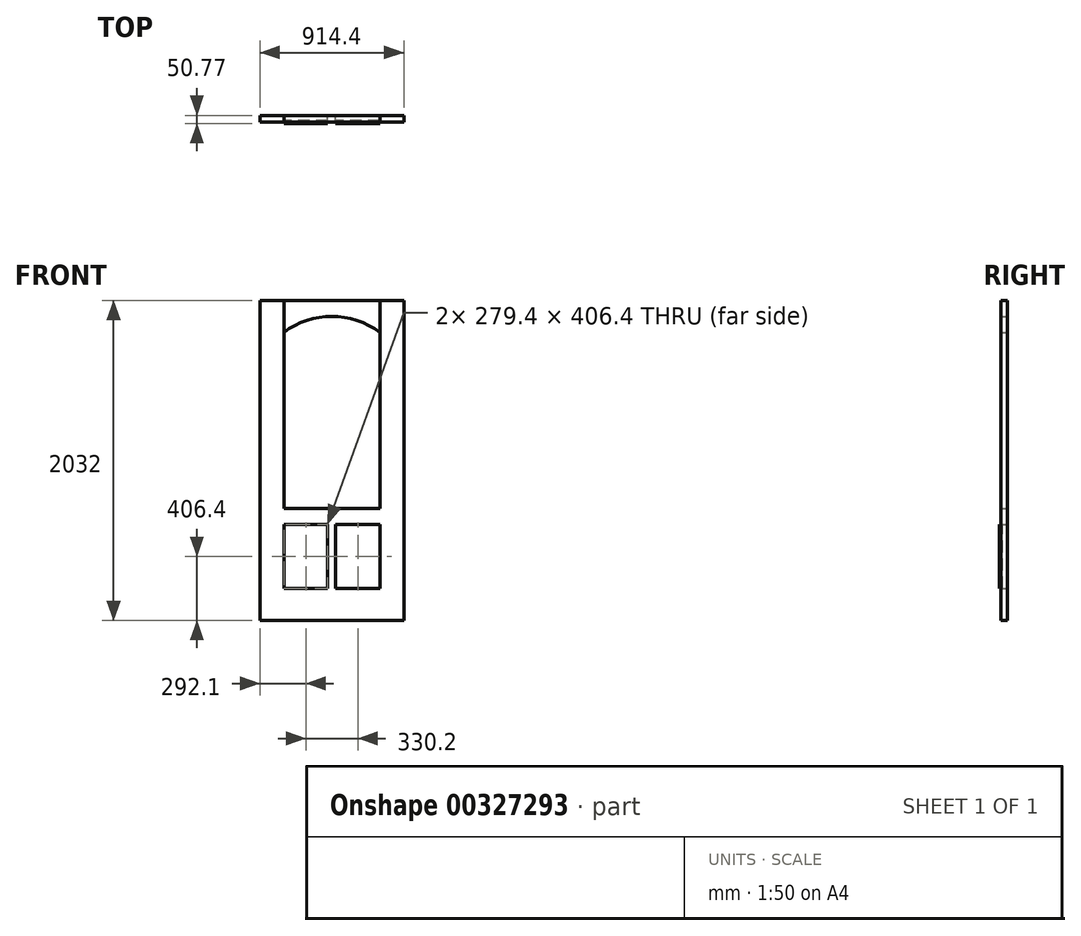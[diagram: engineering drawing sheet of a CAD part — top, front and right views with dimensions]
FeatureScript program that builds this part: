
annotation { "Feature Type Name" : "Feature", "Feature Type Description" : "" }
export const myFeature = defineFeature(function(context is Context, id is Id, definition is map)
    precondition{}
    {
        {
            var Q0;
            Q0=qCreatedBy(makeId("Front.planeOp"),FACE);
            var sketch = newSketch(context, id + "F0", { "sketchPlane" : qUnion([Q0])});
            skLineSegment(sketch, "E0.bottom", {"start": v(0, 0) * mm, "end": v(914.4, 0) * mm});
            skLineSegment(sketch, "E0.top", {"start": v(0, 2032) * mm, "end": v(152.4, 2032) * mm});
            skLineSegment(sketch, "E0.left", {"start": v(0, 0) * mm, "end": v(0, 2032) * mm});
            skLineSegment(sketch, "E0.right", {"start": v(914.4, 0) * mm, "end": v(914.4, 2032) * mm});
            skLineSegment(sketch, "E1", {"start": v(152.4, 2032) * mm, "end": v(152.4, 711.2) * mm});
            skLineSegment(sketch, "E2", {"start": v(152.4, 711.2) * mm, "end": v(762, 711.2) * mm});
            skLineSegment(sketch, "E3", {"start": v(762, 711.2) * mm, "end": v(762, 2032) * mm});
            skLineSegment(sketch, "E4.trimOffspring", {"start": v(762, 2032) * mm, "end": v(914.4, 2032) * mm});
            skSolve(sketch);
        }
        {
            var Q0;
            Q0=makeQuery(id+"F0.imprint","IMPRINT",FACE,{"disambiguationData":[TD([[makeQuery(id+"F0.imprint","IMPRINT",EDGE,{"derivedFrom":sQuery(id+"F0.wireOp",EDGE,"E0.bottom")}),1.0]])]});
            extrude(context, id + "F1", {"entities" : qUnion([Q0]), "depth" : 41.27 * mm});
        }
        {
            var Q0;
            Q0=makeQuery(id+"F1.opExtrude","CAP_FACE",FACE,{"disambiguationData":[OSD([sQuery(id+"F0.wireOp",EDGE,"E0.bottom"),sQuery(id+"F0.wireOp",EDGE,"E0.top"),sQuery(id+"F0.wireOp",EDGE,"E0.left"),sQuery(id+"F0.wireOp",EDGE,"E0.right"),sQuery(id+"F0.wireOp",EDGE,"E1"),sQuery(id+"F0.wireOp",EDGE,"E2"),sQuery(id+"F0.wireOp",EDGE,"E3"),sQuery(id+"F0.wireOp",EDGE,"E4.trimOffspring")])],"isStart":false});
            cPlane(context, id + "F2", {"entities" : qUnion([Q0]), "cplaneType" : CPlaneType.OFFSET, "offset" : 13 / 406.4 * mm, "oppositeDirection" : true, "width" : 152.4 * mm, "height" : 152.4 * mm});
        }
        {
            var Q0;
            Q0=qCreatedBy(makeId("Front.planeOp"),FACE);
            var sketch = newSketch(context, id + "F3", { "sketchPlane" : qUnion([Q0])});
            skLineSegment(sketch, "E5.0", {"start": v(152.4, 2032) * mm, "end": v(152.4, 711.2) * mm});
            skLineSegment(sketch, "E6.0", {"start": v(762, 711.2) * mm, "end": v(762, 2032) * mm});
            skLineSegment(sketch, "E7", {"start": v(152.4, 2032) * mm, "end": v(762, 2032) * mm});
            skLineSegment(sketch, "E8", {"start": v(152.4, 2032) * mm, "end": v(152.4, 1828.8) * mm});
            skLineSegment(sketch, "E9", {"start": v(762, 2032) * mm, "end": v(762, 1828.8) * mm});
            skLineSegment(sketch, "E10", {"start": v(152.4, 1930.4) * mm, "end": v(762, 1930.4) * mm, "construction": true});
            skArc(sketch, "E11", {"start": v(762, 1828.8) * mm, "mid": v(457.2, 1930.4) * mm, "end": v(152.4, 1828.8) * mm});
            skSolve(sketch);
        }
        {
            var Q0;
            Q0=makeQuery(id+"F3.imprint","IMPRINT",FACE,{"disambiguationData":[TD([[makeQuery(id+"F3.imprint","IMPRINT",EDGE,{"derivedFrom":sQuery(id+"F3.wireOp",EDGE,"E7")}),-1.0]])]});
            var Q1;
            Q1=makeQuery(id+"F1.opExtrude","CAP_FACE",FACE,{"disambiguationData":[OSD([sQuery(id+"F0.wireOp",EDGE,"E0.bottom"),sQuery(id+"F0.wireOp",EDGE,"E0.top"),sQuery(id+"F0.wireOp",EDGE,"E0.left"),sQuery(id+"F0.wireOp",EDGE,"E0.right"),sQuery(id+"F0.wireOp",EDGE,"E1"),sQuery(id+"F0.wireOp",EDGE,"E2"),sQuery(id+"F0.wireOp",EDGE,"E3"),sQuery(id+"F0.wireOp",EDGE,"E4.trimOffspring")])],"isStart":false});
            extrude(context, id + "F4", {"entities" : qUnion([Q0]), "endBound" : BoundingType.UP_TO_SURFACE, "endBoundEntityFace" : qUnion([Q1]), "depth" : 25.4 * mm});
        }
        {
            var Q0;
            Q0=qCreatedBy(makeId("Front.planeOp"),FACE);
            var sketch = newSketch(context, id + "F5", { "sketchPlane" : qUnion([Q0])});
            skLineSegment(sketch, "E12.bottom", {"start": v(152.4, 609.6) * mm, "end": v(431.8, 609.6) * mm});
            skLineSegment(sketch, "E12.top", {"start": v(152.4, 203.2) * mm, "end": v(431.8, 203.2) * mm});
            skLineSegment(sketch, "E12.left", {"start": v(152.4, 609.6) * mm, "end": v(152.4, 203.2) * mm});
            skLineSegment(sketch, "E12.right", {"start": v(431.8, 609.6) * mm, "end": v(431.8, 203.2) * mm});
            skLineSegment(sketch, "E13.0", {"start": v(152.4, 711.2) * mm, "end": v(762, 711.2) * mm});
            skLineSegment(sketch, "E14.bottom", {"start": v(482.6, 609.6) * mm, "end": v(762, 609.6) * mm});
            skLineSegment(sketch, "E14.top", {"start": v(482.6, 203.2) * mm, "end": v(762, 203.2) * mm});
            skLineSegment(sketch, "E14.left", {"start": v(482.6, 609.6) * mm, "end": v(482.6, 203.2) * mm});
            skLineSegment(sketch, "E14.right", {"start": v(762, 609.6) * mm, "end": v(762, 203.2) * mm});
            skSolve(sketch);
        }
        {
            var Q0;
            Q0=makeQuery(id+"F5.imprint","IMPRINT",FACE,{"disambiguationData":[TD([[makeQuery(id+"F5.imprint","IMPRINT",EDGE,{"derivedFrom":sQuery(id+"F5.wireOp",EDGE,"E14.bottom")}),-1.0]])]});
            var Q1;
            Q1=makeQuery(id+"F5.imprint","IMPRINT",FACE,{"disambiguationData":[TD([[makeQuery(id+"F5.imprint","IMPRINT",EDGE,{"derivedFrom":sQuery(id+"F5.wireOp",EDGE,"E12.bottom")}),-1.0]])]});
            extrude(context, id + "F6", {"entities" : qUnion([Q0, Q1]), "operationType" : NewBodyOperationType.REMOVE, "endBound" : BoundingType.THROUGH_ALL, "depth" : 25.4 * mm});
        }
        {
            var Q0;
            Q0=qCreatedBy(id+"F2.planeOp",FACE);
            var sketch = newSketch(context, id + "F7", { "sketchPlane" : qUnion([Q0])});
            skLineSegment(sketch, "E15.0", {"start": v(152.4, 203.2) * mm, "end": v(152.4, 609.6) * mm});
            skLineSegment(sketch, "E16.0", {"start": v(431.8, 203.2) * mm, "end": v(152.4, 203.2) * mm});
            skLineSegment(sketch, "E17.0", {"start": v(431.8, 203.2) * mm, "end": v(431.8, 609.6) * mm});
            skLineSegment(sketch, "E18.0", {"start": v(431.8, 609.6) * mm, "end": v(152.4, 609.6) * mm});
            skLineSegment(sketch, "E19.0", {"start": v(482.6, 203.2) * mm, "end": v(482.6, 609.6) * mm});
            skLineSegment(sketch, "E20.0", {"start": v(762, 609.6) * mm, "end": v(482.6, 609.6) * mm});
            skLineSegment(sketch, "E21.0", {"start": v(762, 203.2) * mm, "end": v(482.6, 203.2) * mm});
            skLineSegment(sketch, "E22.0", {"start": v(762, 203.2) * mm, "end": v(762, 609.6) * mm});
            skSolve(sketch);
        }
        {
            var Q0;
            Q0=makeQuery(id+"F7.imprint","IMPRINT",FACE,{"disambiguationData":[TD([[makeQuery(id+"F7.imprint","IMPRINT",EDGE,{"derivedFrom":sQuery(id+"F7.wireOp",EDGE,"E15.0")}),-1.0]])]});
            var Q1;
            Q1=makeQuery(id+"F7.imprint","IMPRINT",FACE,{"disambiguationData":[TD([[makeQuery(id+"F7.imprint","IMPRINT",EDGE,{"derivedFrom":sQuery(id+"F7.wireOp",EDGE,"E19.0")}),-1.0]])]});
            extrude(context, id + "F8", {"entities" : qUnion([Q0, Q1]), "endBound" : BoundingType.SYMMETRIC, "depth" : 19.05 * mm});
        }
    });
